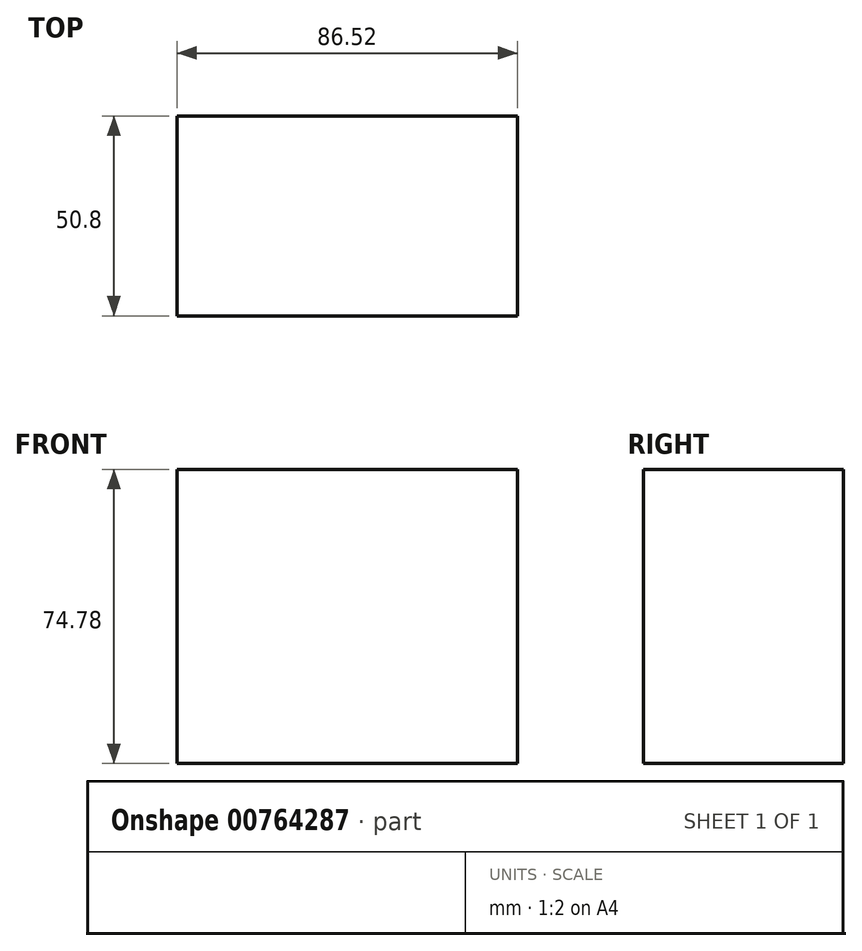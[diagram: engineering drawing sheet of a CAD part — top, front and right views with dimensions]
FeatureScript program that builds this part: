
annotation { "Feature Type Name" : "Feature", "Feature Type Description" : "" }
export const myFeature = defineFeature(function(context is Context, id is Id, definition is map)
    precondition{}
    {
        {
            var Q0;
            Q0=qCreatedBy(makeId("Front.planeOp"),FACE);
            var sketch = newSketch(context, id + "F0", { "sketchPlane" : qUnion([Q0])});
            skLineSegment(sketch, "E0.bottom", {"start": v(43.26, 37.39) * mm, "end": v(-43.26, 37.39) * mm});
            skLineSegment(sketch, "E0.top", {"start": v(43.26, -37.39) * mm, "end": v(-43.26, -37.39) * mm});
            skLineSegment(sketch, "E0.left", {"start": v(43.26, 37.39) * mm, "end": v(43.26, -37.39) * mm});
            skLineSegment(sketch, "E0.right", {"start": v(-43.26, 37.39) * mm, "end": v(-43.26, -37.39) * mm});
            skPoint(sketch, "E0.middle", {"position": v(0, 0) * mm});
            skSolve(sketch);
        }
        {
            var Q0;
            Q0 = qSketchRegion(id + "F0", true);
            var Q1;
            Q1=sQuery(id+"F0.wireOp",EDGE,"E0.bottom");
            var Q2;
            Q2=sQuery(id+"F0.wireOp",EDGE,"E0.right");
            var Q3;
            Q3=sQuery(id+"F0.wireOp",EDGE,"E0.top");
            var Q4;
            Q4=sQuery(id+"F0.wireOp",EDGE,"E0.left");
            extrude(context, id + "F1", {"entities" : qUnion([Q0]), "bodyType" : ToolBodyType.SURFACE, "surfaceEntities" : qUnion([Q1, Q2, Q3, Q4]), "depth" : 50.8 * mm, "offsetDistance" : 25.4 * mm});
        }
    });
